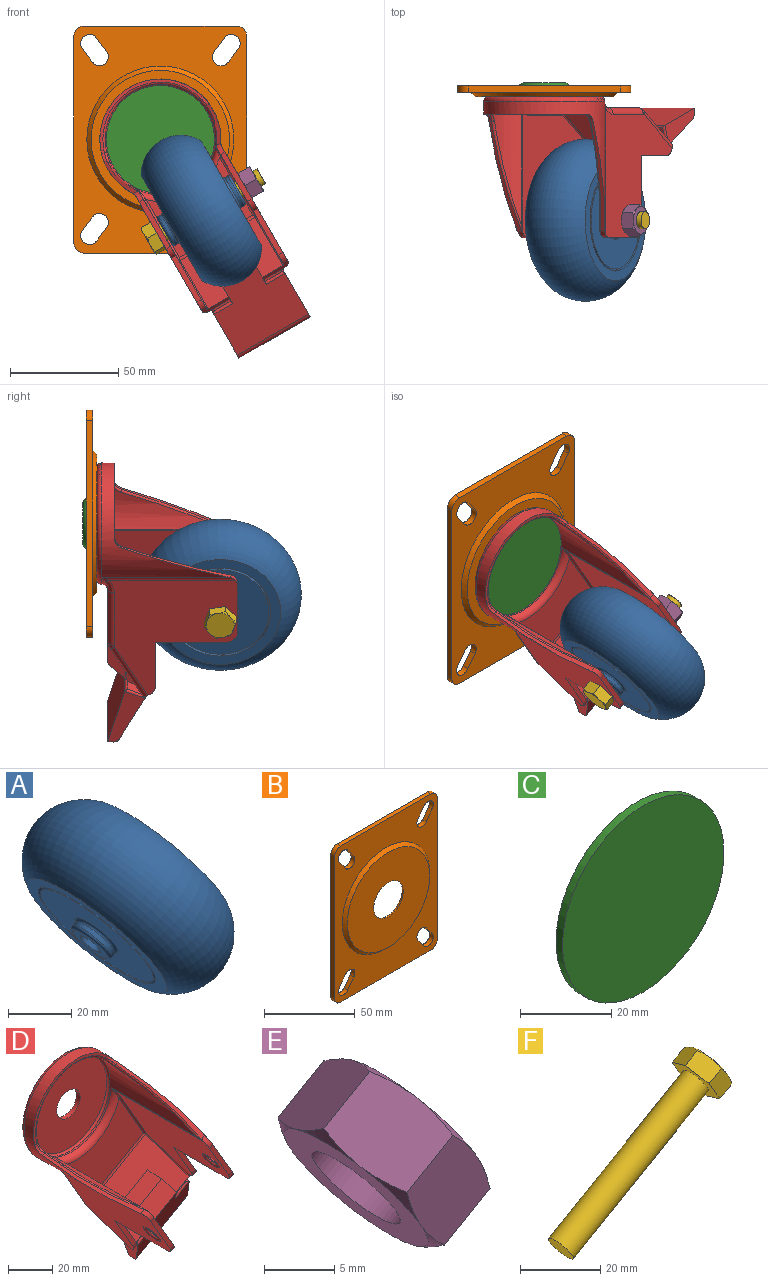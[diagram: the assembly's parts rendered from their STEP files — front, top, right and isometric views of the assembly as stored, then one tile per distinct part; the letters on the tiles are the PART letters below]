
ASSEMBLY  parts=6 mates=10
PART A: 20 faces, bbox 55.7x81.2x70.3 mm
  f0: plane 56x48.51mm, normal (0.87,0,0.5), area 728.1mm2, adj f2,f9
  f1: plane 47x40.71mm, normal (0.87,0,0.5), area 144.5mm2, adj f2,f3
  f2: cylinder r=23.5mm len=47mm, axis (0.87,0,0.5), area 295.3mm2, adj f0,f1
  f3: cylinder r=22.5mm len=45mm, axis (0.87,0,0.5), area 282.7mm2, adj f1,f8
  f4: plane 13.68x11.85mm, normal (0.87,0,0.5), area 96.6mm2, adj f5,f19
  f5: torus R=6.84mm, axis (-0.87,0,-0.5), area 73.8mm2, adj f4,f6
  f6: cylinder r=7.84mm len=15.68mm, axis (-0.87,0,-0.5), area 73.9mm2, adj f5,f7
  f7: torus R=8.84mm, axis (-0.87,0,-0.5), area 80.9mm2, adj f6,f8
  f8: plane 45x38.98mm, normal (0.87,0,0.5), area 1345.1mm2, adj f3,f7
  f9: torus R=19.28mm, axis (-0.87,0,-0.5), area 8394.6mm2, adj f0,f18
  f10: plane 13.68x11.85mm, normal (-0.87,0,-0.5), area 96.6mm2, adj f11,f19
  f11: torus R=6.84mm, axis (-0.87,0,-0.5), area 73.8mm2, adj f10,f12
  f12: cylinder r=7.84mm len=15.68mm, axis (-0.87,0,-0.5), area 73.9mm2, adj f11,f13
  f13: torus R=8.84mm, axis (-0.87,0,-0.5), area 80.9mm2, adj f12,f14
  f14: plane 45x38.98mm, normal (-0.87,0,-0.5), area 1345.1mm2, adj f13,f15
  f15: cylinder r=22.5mm len=45mm, axis (-0.87,0,-0.5), area 282.7mm2, adj f14,f16
  f16: plane 47x40.71mm, normal (-0.87,0,-0.5), area 144.5mm2, adj f15,f17
  f17: cylinder r=23.5mm len=47mm, axis (-0.87,0,-0.5), area 295.3mm2, adj f16,f18
  f18: plane 56x48.51mm, normal (-0.87,0,-0.5), area 728.1mm2, adj f9,f17
  f19: cylinder r=4mm len=37.78mm, axis (-0.87,0,-0.5), area 980.2mm2, adj f4,f10
PART B: 35 faces, bbox 80x6.4x105 mm
  f0: plane 105x80mm, normal (0,1,0), area 4694.5mm2, adj f3,f4,f5,f6,f7,f8,f9,f10
  f1: plane 105x80mm, normal (0,-1,0), area 4279.8mm2, adj f3,f4,f5,f6,f7,f8,f9,f10
  f2: plane 58x58mm, normal (0,1,0), area 518.4mm2, adj f13,f17
  f3: cylinder r=5mm len=5mm, axis (0,-1,0), area 23.6mm2, adj f0,f1,f4,f10
  f4: plane 70x3mm, normal (0,0,1), area 210mm2, adj f0,f1,f3,f5
  f5: cylinder r=5mm len=5mm, axis (0,-1,0), area 23.6mm2, adj f0,f1,f4,f6
  f6: plane 95x3mm, normal (1,0,0), area 285mm2, adj f0,f1,f5,f7
  f7: cylinder r=5mm len=5mm, axis (0,-1,0), area 23.6mm2, adj f0,f1,f6,f8
  f8: plane 70x3mm, normal (0,0,-1), area 210mm2, adj f0,f1,f7,f9
  f9: cylinder r=5mm len=5mm, axis (0,-1,0), area 23.6mm2, adj f0,f1,f8,f10
  f10: plane 95x3mm, normal (-1,0,0), area 285mm2, adj f0,f1,f3,f9
  f11: cone r=34mm half-angle=45deg, axis (0,1,0), area 586.5mm2, adj f1,f12
  f12: plane 64x64mm, normal (0,-1,0), area 2801.5mm2, adj f11,f18
  f13: torus R=32mm, axis (0,-1,0), area 890.9mm2, adj f0,f2
  f14: plane 46x46mm, normal (0,1,0), area 276.5mm2, adj f16,f17
  f15: plane 36x36mm, normal (0,1,0), area 445.3mm2, adj f16,f18
  f16: torus R=21mm, axis (0,1,0), area 565.2mm2, adj f14,f15
  f17: torus R=23mm, axis (0,1,0), area 737.6mm2, adj f2,f14
  f18: torus R=13.5mm, axis (0,1,0), area 241.3mm2, adj f12,f15
  f19: cylinder r=4.1mm len=7.4mm, axis (0,1,0), area 38.6mm2, adj f0,f1,f20,f22
  f20: plane 6.28x4.63mm, normal (-0.81,0,0.59), area 23.4mm2, adj f0,f1,f19,f21
  f21: cylinder r=4.1mm len=7.4mm, axis (0,1,0), area 38.6mm2, adj f0,f1,f20,f22
  f22: plane 6.28x4.63mm, normal (0.81,0,-0.59), area 23.4mm2, adj f0,f1,f19,f21
  f23: cylinder r=4.1mm len=7.4mm, axis (0,1,0), area 38.6mm2, adj f0,f1,f24,f26
  f24: plane 6.28x4.63mm, normal (-0.81,0,-0.59), area 23.4mm2, adj f0,f1,f23,f25
  f25: cylinder r=4.1mm len=7.4mm, axis (0,1,0), area 38.6mm2, adj f0,f1,f24,f26
  f26: plane 6.28x4.63mm, normal (0.81,0,0.59), area 23.4mm2, adj f0,f1,f23,f25
  f27: cylinder r=4.1mm len=7.4mm, axis (0,1,0), area 38.6mm2, adj f0,f1,f28,f30
  f28: plane 6.28x4.63mm, normal (0.81,0,0.59), area 23.4mm2, adj f0,f1,f27,f29
  f29: cylinder r=4.1mm len=7.4mm, axis (0,1,0), area 38.6mm2, adj f0,f1,f28,f30
  f30: plane 6.28x4.63mm, normal (-0.81,0,-0.59), area 23.4mm2, adj f0,f1,f27,f29
  f31: cylinder r=4.1mm len=7.4mm, axis (0,1,0), area 38.6mm2, adj f0,f1,f32,f34
  f32: plane 6.28x4.63mm, normal (0.81,0,-0.59), area 23.4mm2, adj f0,f1,f31,f33
  f33: cylinder r=4.1mm len=7.4mm, axis (0,1,0), area 38.6mm2, adj f0,f1,f32,f34
  f34: plane 6.28x4.63mm, normal (-0.81,0,0.59), area 23.4mm2, adj f0,f1,f31,f33
PART C: 7 faces, bbox 50x11x50 mm
  f0: cylinder r=11mm len=22mm, axis (0,1,0), area 414.7mm2, adj f1,f4
  f1: plane 24x24mm, normal (0,-1,0), area 72.3mm2, adj f0,f3
  f2: plane 18x18mm, normal (0,1,0), area 254.5mm2, adj f3
  f3: torus R=9mm, axis (0,1,0), area 323mm2, adj f1,f2
  f4: plane 50x50mm, normal (0,1,0), area 1583.4mm2, adj f0,f5
  f5: cylinder r=25mm len=50mm, axis (0,-1,0), area 314.2mm2, adj f4,f6
  f6: plane 50x50mm, normal (0,-1,0), area 1963.5mm2, adj f5
PART D: 111 faces, bbox 100.7x67.3x132.4 mm
  f0: plane 23.21x22mm, normal (-0.87,0,-0.5), area 214.2mm2, adj f4,f5,f7,f8,f10,f12,f87,f88
  f1: plane 2.43x1.03mm, normal (0.87,0,0.5), area 1.4mm2, adj f3,f7,f88
  f2: plane 2.43x1.03mm, normal (-0.87,0,-0.5), area 1.4mm2, adj f3,f7,f88
  f3: plane 16.1x9.88mm, normal (0.43,-0.51,-0.75), area 36.1mm2, adj f1,f2,f7,f88
  f4: plane 47.55x42.35mm, normal (0.25,0.86,-0.44), area 792.9mm2, adj f0,f5,f6,f10,f11,f12,f13,f63
  f5: plane 13.18x7.23mm, normal (0.43,-0.51,-0.75), area 35.9mm2, adj f0,f4,f7,f15,f30,f38,f69,f77
  f6: plane 12.08x8.83mm, normal (0.43,-0.51,-0.75), area 35.9mm2, adj f4,f7,f31,f39,f62,f64,f75,f89
  f7: plane 47.55x42.35mm, normal (-0.25,-0.86,0.44), area 876.2mm2, adj f0,f1,f2,f3,f5,f6,f74,f75
  f8: cylinder r=4mm len=8.03mm, axis (-0.87,0,-0.5), area 43.8mm2, adj f0,f10,f12,f86
  f9: cylinder r=4mm len=8.03mm, axis (-0.87,0,-0.5), area 43.8mm2, adj f11,f13,f85,f89
  f10: cylinder r=1mm len=4.09mm, axis (-0.87,0,-0.5), area 5.5mm2, adj f0,f4,f8,f86
  f11: cylinder r=1mm len=4.09mm, axis (-0.87,0,-0.5), area 5.5mm2, adj f4,f9,f85,f89
  f12: cylinder r=1mm len=3.71mm, axis (-0.87,0,-0.5), area 5.5mm2, adj f0,f4,f8,f86
  f13: cylinder r=1mm len=3.71mm, axis (-0.87,0,-0.5), area 5.5mm2, adj f4,f9,f85,f89
  f14: plane 21.63x13.86mm, normal (0,-1,0), area 56.6mm2, adj f15,f16,f30,f38
  f15: cylinder r=5mm len=4.93mm, axis (0.87,0,0.5), area 12.4mm2, adj f5,f14,f30,f38
  f16: plane 33x2.08mm, normal (0.5,0,-0.87), area 79.2mm2, adj f14,f30,f34,f38
  f17: plane 33x2.08mm, normal (0.5,0,-0.87), area 79.2mm2, adj f25,f31,f39,f61
  f18: plane 22.86x14.57mm, normal (0,-1,0), area 60mm2, adj f19,f30,f34,f38
  f19: cylinder r=5mm len=5.49mm, axis (-0.87,0,-0.5), area 14.9mm2, adj f18,f23,f30,f38,f41,f54
  f20: plane 47.44x34.73mm, normal (0,-1,0), area 98.1mm2, adj f21,f22,f27,f52
  f21: cylinder r=5mm len=5.26mm, axis (-0.87,0,-0.5), area 8.5mm2, adj f20,f24,f27,f51
  f22: cylinder r=5mm len=5.26mm, axis (-0.87,0,-0.5), area 8.5mm2, adj f20,f23,f27,f53
  f23: plane 52.59x17.2mm, normal (-0.47,-0.34,0.81), area 92.9mm2, adj f19,f22,f27,f41,f55
  f24: plane 52.59x21.45mm, normal (-0.47,-0.34,0.81), area 92.9mm2, adj f21,f27,f33,f43,f50
  f25: cylinder r=5mm len=5.53mm, axis (-0.87,0,-0.5), area 18.8mm2, adj f17,f26,f31,f39
  f26: plane 22.86x14.57mm, normal (0,-1,0), area 60mm2, adj f25,f31,f33,f39
  f27: cylinder r=28mm len=59.56mm, axis (0,1,0), area 1827.6mm2, adj f20,f21,f22,f23,f24,f32,f41,f43
  f28: plane 52x52mm, normal (0,1,0), area 1947mm2, adj f32,f40
  f29: plane 48.61x44.19mm, normal (0,1,0), area 917.7mm2, adj f42,f63,f66,f71
  f30: plane 59.44x53.35mm, normal (-0.87,0,-0.5), area 2139.6mm2, adj f5,f14,f15,f16,f18,f19,f34,f41
  f31: plane 59.44x53.36mm, normal (0.87,0,0.5), area 2139.6mm2, adj f6,f17,f25,f26,f33,f43,f57,f61
  f32: torus R=26mm, axis (0,1,0), area 538.4mm2, adj f27,f28,f42
  f33: cylinder r=5mm len=5.49mm, axis (-0.87,0,-0.5), area 14.9mm2, adj f24,f26,f31,f39,f43,f48
  f34: cylinder r=5mm len=5.53mm, axis (-0.87,0,-0.5), area 18.8mm2, adj f16,f18,f30,f38
  f35: cylinder r=25.6mm len=56mm, axis (0,1,0), area 1491.1mm2, adj f46,f47,f49,f50,f51,f52,f53,f55
  f36: plane 49.2x49.2mm, normal (0,-1,0), area 1724.5mm2, adj f40,f47
  f37: plane 49.35x46.27mm, normal (0,-1,0), area 998.1mm2, adj f46,f74,f79,f82
  f38: plane 58.88x54.56mm, normal (0.87,0,0.5), area 2198mm2, adj f5,f14,f15,f16,f18,f19,f34,f54
  f39: plane 58.88x54.56mm, normal (-0.87,0,-0.5), area 2198mm2, adj f6,f17,f25,f26,f33,f48,f49,f58
  f40: cylinder r=7.5mm len=15mm, axis (0,1,0), area 113.1mm2, adj f28,f36
  f41: cylinder r=3mm len=61.91mm, axis (0,1,0), area 102.2mm2, adj f19,f23,f27,f30,f73
  f42: torus R=31mm, axis (0,-1,0), area 230.9mm2, adj f29,f32,f67,f68,f72,f73
  f43: cylinder r=3mm len=61.91mm, axis (0,1,0), area 102.2mm2, adj f24,f27,f31,f33,f68
  f44: cylinder r=4mm len=8mm, axis (-0.87,0,-0.5), area 10.1mm2, adj f57,f58
  f45: cylinder r=4mm len=8mm, axis (-0.87,0,-0.5), area 10.1mm2, adj f59,f60
  f46: torus R=28.6mm, axis (0,-1,0), area 214.8mm2, adj f35,f37,f80,f81,f83,f84
  f47: torus R=24.6mm, axis (0,1,0), area 249.1mm2, adj f35,f36
  f48: bspline ~2.3x1.74mm, area 0.4mm2, adj f33,f39,f49,f50
  f49: cylinder r=1mm len=57.69mm, axis (0,1,0), area 34.6mm2, adj f35,f39,f48,f50,f84
  f50: bspline ~50.76x19.3mm, area 70.2mm2, adj f24,f35,f48,f49,f51
  f51: bspline ~5.79x5.08mm, area 10.7mm2, adj f21,f35,f50,f52
  f52: torus R=26.6mm, axis (0,1,0), area 104mm2, adj f20,f35,f51,f53
  f53: bspline ~6.9x5.38mm, area 10.7mm2, adj f22,f35,f52,f55
  f54: bspline ~1.99x1.72mm, area 0.4mm2, adj f19,f38,f55,f56
  f55: bspline ~50.76x14.74mm, area 70.2mm2, adj f23,f35,f53,f54,f56
  f56: cylinder r=1mm len=57.69mm, axis (0,1,0), area 34.6mm2, adj f35,f38,f54,f55,f81
  f57: torus R=5mm, axis (-0.87,0,-0.5), area 43.1mm2, adj f31,f44
  f58: torus R=5mm, axis (-0.87,0,-0.5), area 43.1mm2, adj f39,f44
  f59: torus R=5mm, axis (0.87,0,0.5), area 43.1mm2, adj f30,f45
  f60: torus R=5mm, axis (0.87,0,0.5), area 43.1mm2, adj f38,f45
  f61: plane 21.63x13.86mm, normal (0,-1,0), area 56.6mm2, adj f17,f31,f39,f62
  f62: cylinder r=5mm len=4.93mm, axis (0.87,0,0.5), area 12.4mm2, adj f6,f31,f39,f61
  f63: cylinder r=5mm len=35.92mm, axis (0.87,0,0.5), area 106.9mm2, adj f4,f29,f65,f70
  f64: cylinder r=3mm len=25.19mm, axis (-0.43,0.51,0.75), area 141.4mm2, adj f4,f6,f31,f65
  f65: torus R=2mm, axis (-0.87,0,-0.5), area 9.8mm2, adj f31,f63,f64,f66
  f66: cylinder r=3mm len=25.71mm, axis (0.5,0,-0.87), area 131.7mm2, adj f29,f31,f65,f67
  f67: bspline ~8.87x4.66mm, area 23.2mm2, adj f31,f42,f66,f68
  f68: bspline ~4.57x4.55mm, area 3.3mm2, adj f42,f43,f67
  f69: cylinder r=3mm len=23.04mm, axis (-0.43,0.51,0.75), area 141.4mm2, adj f4,f5,f30,f70
  f70: torus R=2mm, axis (0.87,0,0.5), area 9.8mm2, adj f30,f63,f69,f71
  f71: cylinder r=3mm len=25.71mm, axis (0.5,0,-0.87), area 131.7mm2, adj f29,f30,f70,f72
  f72: bspline ~7.51x6.99mm, area 23.2mm2, adj f30,f42,f71,f73
  f73: bspline ~4.55x3.74mm, area 3.3mm2, adj f41,f42,f72
  f74: cylinder r=2.6mm len=35.31mm, axis (0.87,0,0.5), area 55.3mm2, adj f7,f37,f76,f78,f79,f82
  f75: cylinder r=0.6mm len=22.93mm, axis (-0.43,0.51,0.75), area 28.2mm2, adj f6,f7,f39,f76,f82
  f76: torus R=2mm, axis (-0.87,0,-0.5), area 0.2mm2, adj f74,f75,f82
  f77: cylinder r=0.6mm len=22.5mm, axis (-0.43,0.51,0.75), area 28.2mm2, adj f5,f7,f38,f78,f79
  f78: torus R=2mm, axis (0.87,0,0.5), area 0.2mm2, adj f74,f77,f79
  f79: cylinder r=1mm len=28.24mm, axis (-0.5,0,0.87), area 49.7mm2, adj f37,f38,f74,f77,f78,f80
  f80: bspline ~6.06x4.41mm, area 6.5mm2, adj f38,f46,f79,f81
  f81: bspline ~1.85x1.03mm, area 0.5mm2, adj f46,f56,f80
  f82: cylinder r=1mm len=28.24mm, axis (-0.5,0,0.87), area 49.7mm2, adj f37,f39,f74,f75,f76,f83
  f83: bspline ~6.48x3.5mm, area 6.5mm2, adj f39,f46,f82,f84
  f84: bspline ~1.85x1.3mm, area 0.5mm2, adj f46,f49,f83
  f85: plane 7.3x6.49mm, normal (0.87,0,0.5), area 25.4mm2, adj f4,f9,f11,f13
  f86: plane 7.3x6.49mm, normal (-0.87,0,-0.5), area 25.4mm2, adj f4,f8,f10,f12
  f87: plane 15.61x9.03mm, normal (-0.5,-0.07,0.86), area 10.5mm2, adj f0,f4,f89,f97
  f88: plane 15.92x9.85mm, normal (-0.5,-0.07,0.86), area 177.7mm2, adj f0,f1,f2,f3,f89,f96
  f89: plane 23.21x22mm, normal (0.87,0,0.5), area 214.2mm2, adj f4,f6,f7,f9,f11,f13,f87,f88
  f90: plane 15.59x8.99mm, normal (-0.5,0,0.87), area 18mm2, adj f0,f89,f91,f97
  f91: plane 21.95x20.02mm, normal (0,1,0), area 229.2mm2, adj f0,f89,f90,f102
  f92: plane 18.52x14.07mm, normal (0.36,0.7,-0.62), area 151.4mm2, adj f0,f89,f102,f103
  f93: plane 46.38x42.32mm, normal (-0.14,0.96,0.24), area 1054.3mm2, adj f0,f89,f94,f99,f101,f103,f107,f110
  f94: plane 32.92x18.99mm, normal (0.5,0,-0.87), area 103.7mm2, adj f93,f99,f101,f104
  f95: plane 43.73x40.4mm, normal (0.24,-0.88,-0.42), area 1118.4mm2, adj f0,f89,f96,f99,f101,f104,f105,f108
  f96: plane 19.9x16.46mm, normal (-0.25,-0.86,0.43), area 179.3mm2, adj f0,f88,f89,f95
  f97: plane 19.89x16.45mm, normal (-0.25,-0.86,0.44), area 180mm2, adj f0,f87,f89,f90
  f98: plane 9.28x7.41mm, normal (-0.46,-0.37,0.8), area 71.8mm2, adj f0,f108,f109,f110
  f99: plane 23.41x17.23mm, normal (-0.87,0,-0.5), area 192.2mm2, adj f93,f94,f95,f104,f108,f109,f110
  f100: plane 9.28x7.41mm, normal (-0.46,-0.37,0.8), area 71.8mm2, adj f89,f105,f106,f107
  f101: plane 23.41x17.23mm, normal (0.87,0,0.5), area 192.2mm2, adj f93,f94,f95,f104,f105,f106,f107
  f102: cylinder r=3mm len=16.67mm, axis (0.87,0,0.5), area 43.2mm2, adj f0,f89,f91,f92
  f103: cylinder r=3mm len=17.09mm, axis (-0.87,0,-0.5), area 58.6mm2, adj f0,f89,f92,f93
  f104: cylinder r=3mm len=33.7mm, axis (0.87,0,0.5), area 122.1mm2, adj f94,f95,f99,f101
  f105: cylinder r=1mm len=9.37mm, axis (0.87,0,0.5), area 16.3mm2, adj f89,f95,f100,f101,f106
  f106: cylinder r=1mm len=9.64mm, axis (0.19,-0.93,-0.32), area 14.1mm2, adj f100,f101,f105,f107
  f107: cylinder r=1mm len=9.02mm, axis (0.87,0,0.5), area 16.1mm2, adj f89,f93,f100,f101,f106
  f108: cylinder r=1mm len=9.37mm, axis (0.87,0,0.5), area 16.3mm2, adj f0,f95,f98,f99,f109
  f109: cylinder r=1mm len=9.64mm, axis (-0.19,0.93,0.32), area 14.1mm2, adj f98,f99,f108,f110
  f110: cylinder r=1mm len=9.02mm, axis (0.87,0,0.5), area 16.1mm2, adj f0,f93,f98,f99,f109
PART E: 21 faces, bbox 12.7x15.5x16.2 mm
  f0: plane 9.71x8.92mm, normal (0,-1,0), area 45.8mm2, adj f1,f5,f6,f7,f9,f10,f15,f16
  f1: plane 7.05x7.04mm, normal (0.43,-0.5,-0.75), area 45.8mm2, adj f0,f2,f6,f7,f10,f11,f16,f17
  f2: plane 7.04x7.04mm, normal (0.43,0.5,-0.75), area 45.8mm2, adj f1,f3,f6,f7,f11,f12,f17,f18
  f3: plane 9.71x8.92mm, normal (0,1,0), area 45.8mm2, adj f2,f4,f6,f7,f12,f13,f18,f19
  f4: plane 7.05x7.04mm, normal (-0.43,0.5,0.75), area 45.8mm2, adj f3,f5,f6,f7,f13,f14,f19,f20
  f5: plane 7.04x7.04mm, normal (-0.43,-0.5,0.75), area 45.8mm2, adj f0,f4,f6,f7,f9,f14,f15,f20
  f6: plane 13x11.27mm, normal (0.87,0,0.5), area 82.7mm2, adj f0,f1,f2,f3,f4,f5,f8,f9
  f7: plane 13x11.27mm, normal (-0.87,0,-0.5), area 82.7mm2, adj f0,f1,f2,f3,f4,f5,f8,f15
  f8: cylinder r=4mm len=10.18mm, axis (0.87,0,0.5), area 163.4mm2, adj f6,f7
  f9: cone r=6.51mm half-angle=60deg, axis (-0.87,0,-0.5), area 3.8mm2, adj f0,f5,f6
  f10: cone r=6.51mm half-angle=60deg, axis (-0.87,0,-0.5), area 3.8mm2, adj f0,f1,f6
  f11: cone r=6.51mm half-angle=60deg, axis (-0.87,0,-0.5), area 3.8mm2, adj f1,f2,f6
  f12: cone r=6.51mm half-angle=60deg, axis (-0.87,0,-0.5), area 3.8mm2, adj f2,f3,f6
  f13: cone r=6.51mm half-angle=60deg, axis (-0.87,0,-0.5), area 3.8mm2, adj f3,f4,f6
  f14: cone r=6.51mm half-angle=60deg, axis (-0.87,0,-0.5), area 3.8mm2, adj f4,f5,f6
  f15: cone r=7.51mm half-angle=60deg, axis (0.87,0,0.5), area 3.8mm2, adj f0,f5,f7
  f16: cone r=7.51mm half-angle=60deg, axis (0.87,0,0.5), area 3.8mm2, adj f0,f1,f7
  f17: cone r=7.51mm half-angle=60deg, axis (0.87,0,0.5), area 3.8mm2, adj f1,f2,f7
  f18: cone r=7.51mm half-angle=60deg, axis (0.87,0,0.5), area 3.8mm2, adj f2,f3,f7
  f19: cone r=7.51mm half-angle=60deg, axis (0.87,0,0.5), area 3.8mm2, adj f3,f4,f7
  f20: cone r=7.51mm half-angle=60deg, axis (0.87,0,0.5), area 3.8mm2, adj f4,f5,f7
PART F: 16 faces, bbox 58.2x15.6x40.5 mm
  f0: plane 13x13mm, normal (-0.87,0,-0.5), area 96.1mm2, adj f1,f2,f3,f4,f5,f6,f14
  f1: plane 9.55x8.58mm, normal (0,-1,0), area 39.4mm2, adj f0,f2,f6,f7,f8
  f2: plane 7.12x6.71mm, normal (0.43,-0.5,-0.75), area 39.4mm2, adj f0,f1,f3,f8,f9
  f3: plane 7.13x6.71mm, normal (0.43,0.5,-0.75), area 39.4mm2, adj f0,f2,f4,f9,f10
  f4: plane 9.55x8.58mm, normal (0,1,0), area 39.4mm2, adj f0,f3,f5,f10,f11
  f5: plane 7.12x6.71mm, normal (-0.43,0.5,0.75), area 39.4mm2, adj f0,f4,f6,f11,f12
  f6: plane 7.13x6.71mm, normal (-0.43,-0.5,0.75), area 39.4mm2, adj f0,f1,f5,f7,f12
  f7: cone r=6.5mm half-angle=60deg, axis (-0.87,0,-0.5), area 4.2mm2, adj f1,f6,f13
  f8: cone r=6.5mm half-angle=60deg, axis (-0.87,0,-0.5), area 4.2mm2, adj f1,f2,f13
  f9: cone r=6.5mm half-angle=60deg, axis (-0.87,0,-0.5), area 4.2mm2, adj f2,f3,f13
  f10: cone r=6.5mm half-angle=60deg, axis (-0.87,0,-0.5), area 4.2mm2, adj f3,f4,f13
  f11: cone r=6.5mm half-angle=60deg, axis (-0.87,0,-0.5), area 4.2mm2, adj f4,f5,f13
  f12: cone r=6.5mm half-angle=60deg, axis (-0.87,0,-0.5), area 4.2mm2, adj f5,f6,f13
  f13: plane 13x11.26mm, normal (0.87,0,0.5), area 132.7mm2, adj f7,f8,f9,f10,f11,f12
  f14: cylinder r=4mm len=51.64mm, axis (0.87,0,0.5), area 1382.3mm2, adj f0,f15
  f15: plane 8x6.93mm, normal (-0.87,0,-0.5), area 50.3mm2, adj f14
PLACE A rot(axis=(-0.32,0.77,0.55),180deg) t=(145.77,-575.09,264.29)mm
PLACE B rot(axis=(0.5,0,-0.87),0deg) t=(150.15,-574.41,263.63)mm
PLACE C rot(axis=(0.5,0,-0.87),0deg) t=(150.15,-572.81,263.63)mm
PLACE D t=(150.15,-572.81,263.63)mm
PLACE E rot(axis=(-0.35,0.71,0.61),180deg) t=(141.78,-583.55,271.2)mm
PLACE F rot(axis=(-0.32,0.77,0.55),180deg) t=(145.77,-575.09,264.29)mm
MATE cylindrical F.f14 <-> A.f6  axis (-0.87,0,-0.5) through (171.04,-620.55,232.96)mm
MATE revolute F.f14 <-> A.f6  axis (-0.87,0,-0.5) through (171.04,-620.55,232.96)mm
MATE planar B.f11 <-> D.f27  axis (0,-1,0) through (148.15,-563.55,263.63)mm
MATE cylindrical C.f0 <-> D.f27  axis (0,1,0) through (148.15,-562.95,263.63)mm
MATE planar C.f0 <-> D.f27  axis (0,1,0) through (148.15,-565.95,263.63)mm
MATE cylindrical E.f9 <-> F.f14  axis (0.87,0,0.5) through (192.69,-620.55,245.45)mm
MATE planar E.f6 <-> D.f31  axis (-0.87,0,-0.5) through (185.44,-614.92,245.02)mm
MATE cylindrical F.f14 <-> D.f58  axis (-0.87,0,-0.5) through (147.21,-620.55,219.22)mm
MATE planar F.f0 <-> D.f30  axis (0.87,0,0.5) through (150.4,-621.79,213.69)mm
MATE cylindrical C.f0 <-> B.f11  axis (0,1,0) through (148.15,-556.95,263.63)mm
